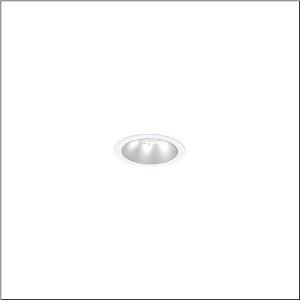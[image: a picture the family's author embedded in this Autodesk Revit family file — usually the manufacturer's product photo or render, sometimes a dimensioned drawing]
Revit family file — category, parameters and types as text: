
# Revit family: lunis_21_s_51db19ma91c
name_source: partatom
category: Lighting Fixtures
units: mm (PartAtom-declared; Revit-internal decimal feet)

## family parameters
Cut with Voids When Loaded = No
Host = Face
Light Source = No
Part Type = Normal
Room Calculation Point = No
Round Connector Dimension = Use Diameter
Shared = No

## types (1)
- --- (1 x LED, 930 lm, 5.9 W, 6500K)
    Apparent Load = 6 VA
    CIE Flux Codes = 90 98 100 100 100
    Color Rendering = 80
    Color Temperature = 6500K
    Default Elevation = 1800 mm
    Description = Lunis 21 S, downlight, light control with lens, of PMMA, anti glare with reflector, of PC, matt, light emission: direct distribution, LED rated luminous flux: 940lm, light colour: 830/840/865, with terminal, 3-pole, mains connection: 220..240V, AC, 50..60Hz, housing, round, of diecast aluminium, traffic white (RAL 9016), diameter: 84mm, clamping range: 1..40mm, protection rating (complete): IP20, protection rating (on room side): IP54, insulation class (complete): insulation class II (safety insulation), certification: CE, impact resistance: IK03, packaging unit: 1 piece
    Height = 0 mm  [stored 0 ft]
    Lamp = 1 x LED
    Lamp Light Flux = 930 lm
    Lamp Power = 5.9 W
    Lamp count = 1
    Length = 84 mm
    Luminous efficacy = 158 lm/W
    Manufacturer = Siteco
    ModVariant = No
    Model = 51DB19MA91C
    Mounting Place = Ceiling
    Mounting Type = Recessed
    Number of Poles = 1
    OnlyDefault = Yes
    Power Factor = 1
    Product Name = Lunis 21 S
    Product group = downlight
    ProductGroupID = 401
    Protection Class = Protection class II
    Protection Degree = IP 20
    RLX_Detail_Level = 1
    RLX_Emergency_Light_Flux = 0 lm
    RLX_Emergency_Type = 0
    RLX_Emergency_Type_DB = No
    RlxData = <blob elided: 8577 chars, md5=9e669ed1>
    Socket = socket
    Standby Power = 0 W
    System Light Flux = 930 lm
    System Power = 6 W
    Type Comments = individual setting: colour temperature 6500K
    Type Image = l_1290846.jpg
    URL = http://relux.com
    VarID = @adj_035057
    Voltage = 0 V
    Weight = 0.00 kg
    Width = 0 mm  [stored 0 ft]

note: [stored X ft] marks values corroborated as IEEE doubles in the binary element streams (Revit-internal decimal feet)

## geometry (parser evidence)
native form markers: Sweep x10
no freeform markers — native parametric forms only
